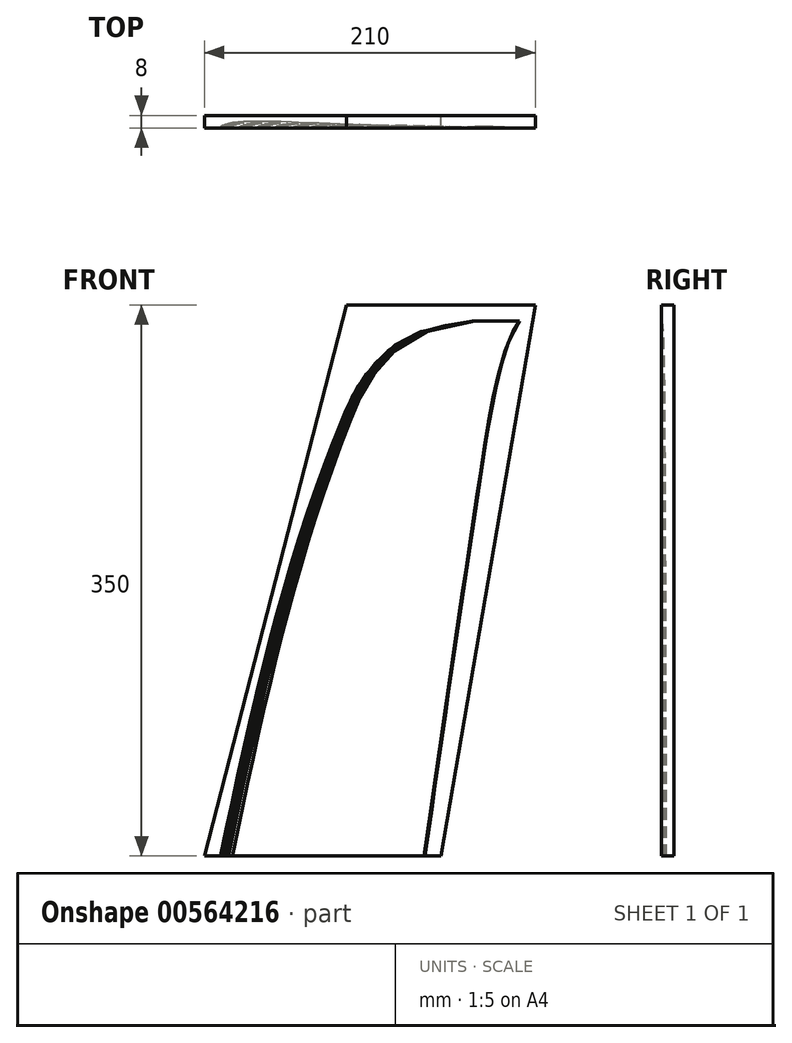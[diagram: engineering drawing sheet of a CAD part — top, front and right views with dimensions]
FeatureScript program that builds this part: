
annotation { "Feature Type Name" : "Feature", "Feature Type Description" : "" }
export const myFeature = defineFeature(function(context is Context, id is Id, definition is map)
    precondition{}
    {
        {
            var Q0;
            Q0=qCreatedBy(makeId("Top.planeOp"),FACE);
            cPlane(context, id + "F0", {"entities" : qUnion([Q0]), "cplaneType" : CPlaneType.OFFSET, "offset" : 250 * mm, "width" : 150 * mm, "height" : 150 * mm});
        }
        {
            var Q0;
            Q0=qCreatedBy(makeId("Top.planeOp"),FACE);
            cPlane(context, id + "F1", {"entities" : qUnion([Q0]), "cplaneType" : CPlaneType.OFFSET, "offset" : 300 * mm, "width" : 150 * mm, "height" : 150 * mm});
        }
        {
            var Q0;
            Q0=qCreatedBy(makeId("Top.planeOp"),FACE);
            cPlane(context, id + "F2", {"entities" : qUnion([Q0]), "cplaneType" : CPlaneType.OFFSET, "offset" : 320 * mm, "width" : 150 * mm, "height" : 150 * mm});
        }
        {
            var Q0;
            Q0=qCreatedBy(makeId("Top.planeOp"),FACE);
            cPlane(context, id + "F3", {"entities" : qUnion([Q0]), "cplaneType" : CPlaneType.OFFSET, "offset" : 340 * mm, "width" : 150 * mm, "height" : 150 * mm});
        }
        {
            var Q0;
            Q0=qCreatedBy(makeId("Top.planeOp"),FACE);
            var sketch = newSketch(context, id + "F4", { "sketchPlane" : qUnion([Q0])});
            skLineSegment(sketch, "E0", {"start": v(130, 0.16) * mm, "end": v(129.46, 0.15) * mm});
            skLineSegment(sketch, "E1", {"start": v(129.46, 0.15) * mm, "end": v(128.28, 0.22) * mm});
            skLineSegment(sketch, "E2", {"start": v(128.28, 0.22) * mm, "end": v(126.06, 0.3) * mm});
            skLineSegment(sketch, "E3", {"start": v(126.06, 0.3) * mm, "end": v(123.2, 0.44) * mm});
            skLineSegment(sketch, "E4", {"start": v(123.2, 0.44) * mm, "end": v(119.45, 0.6) * mm});
            skLineSegment(sketch, "E5", {"start": v(119.45, 0.6) * mm, "end": v(115.33, 0.75) * mm});
            skLineSegment(sketch, "E6", {"start": v(115.33, 0.75) * mm, "end": v(110.89, 0.96) * mm});
            skLineSegment(sketch, "E7", {"start": v(110.89, 0.96) * mm, "end": v(106, 1.14) * mm});
            skLineSegment(sketch, "E8", {"start": v(106, 1.14) * mm, "end": v(100.37, 1.42) * mm});
            skLineSegment(sketch, "E9", {"start": v(100.37, 1.42) * mm, "end": v(94.84, 1.6) * mm});
            skLineSegment(sketch, "E10", {"start": v(94.84, 1.6) * mm, "end": v(89.05, 1.89) * mm});
            skLineSegment(sketch, "E11", {"start": v(89.05, 1.89) * mm, "end": v(82.47, 2.15) * mm});
            skLineSegment(sketch, "E12", {"start": v(82.47, 2.15) * mm, "end": v(76.13, 2.4) * mm});
            skLineSegment(sketch, "E13", {"start": v(76.13, 2.4) * mm, "end": v(69.53, 2.68) * mm});
            skLineSegment(sketch, "E14", {"start": v(69.53, 2.68) * mm, "end": v(62.6, 3.03) * mm});
            skLineSegment(sketch, "E15", {"start": v(62.6, 3.03) * mm, "end": v(56.55, 3.26) * mm});
            skLineSegment(sketch, "E16", {"start": v(56.55, 3.26) * mm, "end": v(49.78, 3.57) * mm});
            skLineSegment(sketch, "E17", {"start": v(49.78, 3.57) * mm, "end": v(45.16, 3.74) * mm});
            skLineSegment(sketch, "E18", {"start": v(45.16, 3.74) * mm, "end": v(38.39, 3.98) * mm});
            skLineSegment(sketch, "E19", {"start": v(38.39, 3.98) * mm, "end": v(33.66, 4.1) * mm});
            skLineSegment(sketch, "E20", {"start": v(33.66, 4.1) * mm, "end": v(28.01, 4.2) * mm});
            skLineSegment(sketch, "E21", {"start": v(28.01, 4.2) * mm, "end": v(23.16, 4.22) * mm});
            skLineSegment(sketch, "E22", {"start": v(23.16, 4.22) * mm, "end": v(18.3, 4.15) * mm});
            skLineSegment(sketch, "E23", {"start": v(18.3, 4.15) * mm, "end": v(14.57, 4) * mm});
            skLineSegment(sketch, "E24", {"start": v(14.57, 4) * mm, "end": v(11.21, 3.75) * mm});
            skLineSegment(sketch, "E25", {"start": v(11.21, 3.75) * mm, "end": v(7.63, 3.34) * mm});
            skLineSegment(sketch, "E26", {"start": v(7.63, 3.34) * mm, "end": v(5.05, 2.89) * mm});
            skLineSegment(sketch, "E27", {"start": v(5.05, 2.89) * mm, "end": v(2.92, 2.28) * mm});
            skLineSegment(sketch, "E28", {"start": v(2.92, 2.28) * mm, "end": v(1.32, 1.56) * mm});
            skLineSegment(sketch, "E29", {"start": v(1.32, 1.56) * mm, "end": v(0.49, 0.98) * mm});
            skLineSegment(sketch, "E30", {"start": v(0.49, 0.98) * mm, "end": v(0.08, 0.4) * mm});
            skLineSegment(sketch, "E31", {"start": v(0.08, 0.4) * mm, "end": v(0, 0) * mm});
            skLineSegment(sketch, "E32", {"start": v(0, 0) * mm, "end": v(0.03, -0.22) * mm});
            skLineSegment(sketch, "E33", {"start": v(0.03, -0.22) * mm, "end": v(0.08, -0.45) * mm});
            skLineSegment(sketch, "E34", {"start": v(0.08, -0.45) * mm, "end": v(0.22, -0.67) * mm});
            skLineSegment(sketch, "E35", {"start": v(0.22, -0.67) * mm, "end": v(1, -1.38) * mm});
            skLineSegment(sketch, "E36", {"start": v(1, -1.38) * mm, "end": v(2.07, -1.93) * mm});
            skLineSegment(sketch, "E37", {"start": v(2.07, -1.93) * mm, "end": v(3.73, -2.53) * mm});
            skLineSegment(sketch, "E38", {"start": v(3.73, -2.53) * mm, "end": v(6.34, -3.13) * mm});
            skLineSegment(sketch, "E39", {"start": v(6.34, -3.13) * mm, "end": v(9.36, -3.57) * mm});
            skLineSegment(sketch, "E40", {"start": v(9.36, -3.57) * mm, "end": v(13.18, -3.91) * mm});
            skLineSegment(sketch, "E41", {"start": v(13.18, -3.91) * mm, "end": v(17.57, -4.14) * mm});
            skLineSegment(sketch, "E42", {"start": v(17.57, -4.14) * mm, "end": v(22.67, -4.2) * mm});
            skLineSegment(sketch, "E43", {"start": v(22.67, -4.2) * mm, "end": v(28.18, -4.22) * mm});
            skLineSegment(sketch, "E44", {"start": v(28.18, -4.22) * mm, "end": v(34.02, -4.06) * mm});
            skLineSegment(sketch, "E45", {"start": v(34.02, -4.06) * mm, "end": v(40.18, -3.88) * mm});
            skLineSegment(sketch, "E46", {"start": v(40.18, -3.88) * mm, "end": v(46.73, -3.67) * mm});
            skLineSegment(sketch, "E47", {"start": v(46.73, -3.67) * mm, "end": v(53.52, -3.4) * mm});
            skLineSegment(sketch, "E48", {"start": v(53.52, -3.4) * mm, "end": v(61.2, -3.04) * mm});
            skLineSegment(sketch, "E49", {"start": v(61.2, -3.04) * mm, "end": v(67.7, -2.76) * mm});
            skLineSegment(sketch, "E50", {"start": v(67.7, -2.76) * mm, "end": v(74.25, -2.49) * mm});
            skLineSegment(sketch, "E51", {"start": v(74.25, -2.49) * mm, "end": v(81.45, -2.17) * mm});
            skLineSegment(sketch, "E52", {"start": v(81.45, -2.17) * mm, "end": v(88.16, -1.9) * mm});
            skLineSegment(sketch, "E53", {"start": v(88.16, -1.9) * mm, "end": v(94.61, -1.62) * mm});
            skLineSegment(sketch, "E54", {"start": v(94.61, -1.62) * mm, "end": v(100.76, -1.37) * mm});
            skLineSegment(sketch, "E55", {"start": v(100.76, -1.37) * mm, "end": v(106.42, -1.13) * mm});
            skLineSegment(sketch, "E56", {"start": v(106.42, -1.13) * mm, "end": v(111.7, -0.9) * mm});
            skLineSegment(sketch, "E57", {"start": v(111.7, -0.9) * mm, "end": v(116.1, -0.72) * mm});
            skLineSegment(sketch, "E58", {"start": v(116.1, -0.72) * mm, "end": v(120.1, -0.54) * mm});
            skLineSegment(sketch, "E59", {"start": v(120.1, -0.54) * mm, "end": v(123.41, -0.43) * mm});
            skLineSegment(sketch, "E60", {"start": v(123.41, -0.43) * mm, "end": v(126.23, -0.29) * mm});
            skLineSegment(sketch, "E61", {"start": v(126.23, -0.29) * mm, "end": v(128.2, -0.2) * mm});
            skLineSegment(sketch, "E62", {"start": v(128.2, -0.2) * mm, "end": v(130, -0.13) * mm});
            skLineSegment(sketch, "E63", {"start": v(130, -0.13) * mm, "end": v(130, 0.16) * mm});
            skSolve(sketch);
        }
        {
            var Q0;
            Q0=qCreatedBy(id+"F0.planeOp",FACE);
            var sketch = newSketch(context, id + "F5", { "sketchPlane" : qUnion([Q0])});
            skLineSegment(sketch, "E64", {"start": v(166.6, 0.13) * mm, "end": v(166.18, 0.12) * mm});
            skLineSegment(sketch, "E65", {"start": v(166.18, 0.12) * mm, "end": v(165.27, 0.17) * mm});
            skLineSegment(sketch, "E66", {"start": v(165.27, 0.17) * mm, "end": v(163.56, 0.23) * mm});
            skLineSegment(sketch, "E67", {"start": v(163.56, 0.23) * mm, "end": v(161.37, 0.33) * mm});
            skLineSegment(sketch, "E68", {"start": v(161.37, 0.33) * mm, "end": v(158.49, 0.46) * mm});
            skLineSegment(sketch, "E69", {"start": v(158.49, 0.46) * mm, "end": v(155.31, 0.58) * mm});
            skLineSegment(sketch, "E70", {"start": v(155.31, 0.58) * mm, "end": v(151.9, 0.74) * mm});
            skLineSegment(sketch, "E71", {"start": v(151.9, 0.74) * mm, "end": v(148.14, 0.88) * mm});
            skLineSegment(sketch, "E72", {"start": v(148.14, 0.88) * mm, "end": v(143.8, 1.1) * mm});
            skLineSegment(sketch, "E73", {"start": v(143.8, 1.1) * mm, "end": v(139.55, 1.24) * mm});
            skLineSegment(sketch, "E74", {"start": v(139.55, 1.24) * mm, "end": v(135.1, 1.45) * mm});
            skLineSegment(sketch, "E75", {"start": v(135.1, 1.45) * mm, "end": v(130.04, 1.65) * mm});
            skLineSegment(sketch, "E76", {"start": v(130.04, 1.65) * mm, "end": v(125.16, 1.85) * mm});
            skLineSegment(sketch, "E77", {"start": v(125.16, 1.85) * mm, "end": v(120.08, 2.06) * mm});
            skLineSegment(sketch, "E78", {"start": v(120.08, 2.06) * mm, "end": v(114.76, 2.33) * mm});
            skLineSegment(sketch, "E79", {"start": v(114.76, 2.33) * mm, "end": v(110.1, 2.5) * mm});
            skLineSegment(sketch, "E80", {"start": v(110.1, 2.5) * mm, "end": v(104.9, 2.75) * mm});
            skLineSegment(sketch, "E81", {"start": v(104.9, 2.75) * mm, "end": v(101.34, 2.88) * mm});
            skLineSegment(sketch, "E82", {"start": v(101.34, 2.88) * mm, "end": v(96.13, 3.06) * mm});
            skLineSegment(sketch, "E83", {"start": v(96.13, 3.06) * mm, "end": v(92.5, 3.16) * mm});
            skLineSegment(sketch, "E84", {"start": v(92.5, 3.16) * mm, "end": v(88.15, 3.23) * mm});
            skLineSegment(sketch, "E85", {"start": v(88.15, 3.23) * mm, "end": v(84.42, 3.24) * mm});
            skLineSegment(sketch, "E86", {"start": v(84.42, 3.24) * mm, "end": v(80.69, 3.19) * mm});
            skLineSegment(sketch, "E87", {"start": v(80.69, 3.19) * mm, "end": v(77.81, 3.08) * mm});
            skLineSegment(sketch, "E88", {"start": v(77.81, 3.08) * mm, "end": v(75.23, 2.89) * mm});
            skLineSegment(sketch, "E89", {"start": v(75.23, 2.89) * mm, "end": v(72.47, 2.57) * mm});
            skLineSegment(sketch, "E90", {"start": v(72.47, 2.57) * mm, "end": v(70.5, 2.22) * mm});
            skLineSegment(sketch, "E91", {"start": v(70.5, 2.22) * mm, "end": v(68.85, 1.76) * mm});
            skLineSegment(sketch, "E92", {"start": v(68.85, 1.76) * mm, "end": v(67.62, 1.2) * mm});
            skLineSegment(sketch, "E93", {"start": v(67.62, 1.2) * mm, "end": v(66.98, 0.75) * mm});
            skLineSegment(sketch, "E94", {"start": v(66.98, 0.75) * mm, "end": v(66.66, 0.3) * mm});
            skLineSegment(sketch, "E95", {"start": v(66.66, 0.3) * mm, "end": v(66.6, 0) * mm});
            skLineSegment(sketch, "E96", {"start": v(66.6, 0) * mm, "end": v(66.62, -0.17) * mm});
            skLineSegment(sketch, "E97", {"start": v(66.62, -0.17) * mm, "end": v(66.66, -0.35) * mm});
            skLineSegment(sketch, "E98", {"start": v(66.66, -0.35) * mm, "end": v(66.78, -0.52) * mm});
            skLineSegment(sketch, "E99", {"start": v(66.78, -0.52) * mm, "end": v(67.37, -1.06) * mm});
            skLineSegment(sketch, "E100", {"start": v(67.37, -1.06) * mm, "end": v(68.2, -1.48) * mm});
            skLineSegment(sketch, "E101", {"start": v(68.2, -1.48) * mm, "end": v(69.47, -1.95) * mm});
            skLineSegment(sketch, "E102", {"start": v(69.47, -1.95) * mm, "end": v(71.48, -2.4) * mm});
            skLineSegment(sketch, "E103", {"start": v(71.48, -2.4) * mm, "end": v(73.8, -2.74) * mm});
            skLineSegment(sketch, "E104", {"start": v(73.8, -2.74) * mm, "end": v(76.75, -3) * mm});
            skLineSegment(sketch, "E105", {"start": v(76.75, -3) * mm, "end": v(80.12, -3.18) * mm});
            skLineSegment(sketch, "E106", {"start": v(80.12, -3.18) * mm, "end": v(84.04, -3.23) * mm});
            skLineSegment(sketch, "E107", {"start": v(84.04, -3.23) * mm, "end": v(88.28, -3.24) * mm});
            skLineSegment(sketch, "E108", {"start": v(88.28, -3.24) * mm, "end": v(92.77, -3.12) * mm});
            skLineSegment(sketch, "E109", {"start": v(92.77, -3.12) * mm, "end": v(97.5, -2.99) * mm});
            skLineSegment(sketch, "E110", {"start": v(97.5, -2.99) * mm, "end": v(102.55, -2.82) * mm});
            skLineSegment(sketch, "E111", {"start": v(102.55, -2.82) * mm, "end": v(107.77, -2.62) * mm});
            skLineSegment(sketch, "E112", {"start": v(107.77, -2.62) * mm, "end": v(113.67, -2.34) * mm});
            skLineSegment(sketch, "E113", {"start": v(113.67, -2.34) * mm, "end": v(118.68, -2.12) * mm});
            skLineSegment(sketch, "E114", {"start": v(118.68, -2.12) * mm, "end": v(123.72, -1.91) * mm});
            skLineSegment(sketch, "E115", {"start": v(123.72, -1.91) * mm, "end": v(129.25, -1.67) * mm});
            skLineSegment(sketch, "E116", {"start": v(129.25, -1.67) * mm, "end": v(134.41, -1.46) * mm});
            skLineSegment(sketch, "E117", {"start": v(134.41, -1.46) * mm, "end": v(139.38, -1.24) * mm});
            skLineSegment(sketch, "E118", {"start": v(139.38, -1.24) * mm, "end": v(144.1, -1.06) * mm});
            skLineSegment(sketch, "E119", {"start": v(144.1, -1.06) * mm, "end": v(148.46, -0.87) * mm});
            skLineSegment(sketch, "E120", {"start": v(148.46, -0.87) * mm, "end": v(152.52, -0.7) * mm});
            skLineSegment(sketch, "E121", {"start": v(152.52, -0.7) * mm, "end": v(155.91, -0.56) * mm});
            skLineSegment(sketch, "E122", {"start": v(155.91, -0.56) * mm, "end": v(158.99, -0.42) * mm});
            skLineSegment(sketch, "E123", {"start": v(158.99, -0.42) * mm, "end": v(161.53, -0.33) * mm});
            skLineSegment(sketch, "E124", {"start": v(161.53, -0.33) * mm, "end": v(163.7, -0.22) * mm});
            skLineSegment(sketch, "E125", {"start": v(163.7, -0.22) * mm, "end": v(165.2, -0.15) * mm});
            skLineSegment(sketch, "E126", {"start": v(165.2, -0.15) * mm, "end": v(166.6, -0.1) * mm});
            skLineSegment(sketch, "E127", {"start": v(166.6, -0.1) * mm, "end": v(166.6, 0.13) * mm});
            skSolve(sketch);
        }
        {
            var Q0;
            Q0=qCreatedBy(id+"F1.planeOp",FACE);
            var sketch = newSketch(context, id + "F6", { "sketchPlane" : qUnion([Q0])});
            skLineSegment(sketch, "E128", {"start": v(175.53, 0.1) * mm, "end": v(175.16, 0.1) * mm});
            skLineSegment(sketch, "E129", {"start": v(175.16, 0.1) * mm, "end": v(174.37, 0.15) * mm});
            skLineSegment(sketch, "E130", {"start": v(174.37, 0.15) * mm, "end": v(172.88, 0.2) * mm});
            skLineSegment(sketch, "E131", {"start": v(172.88, 0.2) * mm, "end": v(170.98, 0.3) * mm});
            skLineSegment(sketch, "E132", {"start": v(170.98, 0.3) * mm, "end": v(168.46, 0.4) * mm});
            skLineSegment(sketch, "E133", {"start": v(168.46, 0.4) * mm, "end": v(165.7, 0.5) * mm});
            skLineSegment(sketch, "E134", {"start": v(165.7, 0.5) * mm, "end": v(162.73, 0.64) * mm});
            skLineSegment(sketch, "E135", {"start": v(162.73, 0.64) * mm, "end": v(159.46, 0.76) * mm});
            skLineSegment(sketch, "E136", {"start": v(159.46, 0.76) * mm, "end": v(155.68, 0.95) * mm});
            skLineSegment(sketch, "E137", {"start": v(155.68, 0.95) * mm, "end": v(151.98, 1.08) * mm});
            skLineSegment(sketch, "E138", {"start": v(151.98, 1.08) * mm, "end": v(148.1, 1.26) * mm});
            skLineSegment(sketch, "E139", {"start": v(148.1, 1.26) * mm, "end": v(143.7, 1.44) * mm});
            skLineSegment(sketch, "E140", {"start": v(143.7, 1.44) * mm, "end": v(139.45, 1.61) * mm});
            skLineSegment(sketch, "E141", {"start": v(139.45, 1.61) * mm, "end": v(135.03, 1.8) * mm});
            skLineSegment(sketch, "E142", {"start": v(135.03, 1.8) * mm, "end": v(130.4, 2.03) * mm});
            skLineSegment(sketch, "E143", {"start": v(130.4, 2.03) * mm, "end": v(126.34, 2.18) * mm});
            skLineSegment(sketch, "E144", {"start": v(126.34, 2.18) * mm, "end": v(121.81, 2.4) * mm});
            skLineSegment(sketch, "E145", {"start": v(121.81, 2.4) * mm, "end": v(118.72, 2.5) * mm});
            skLineSegment(sketch, "E146", {"start": v(118.72, 2.5) * mm, "end": v(114.18, 2.66) * mm});
            skLineSegment(sketch, "E147", {"start": v(114.18, 2.66) * mm, "end": v(111.02, 2.75) * mm});
            skLineSegment(sketch, "E148", {"start": v(111.02, 2.75) * mm, "end": v(107.23, 2.81) * mm});
            skLineSegment(sketch, "E149", {"start": v(107.23, 2.81) * mm, "end": v(103.99, 2.82) * mm});
            skLineSegment(sketch, "E150", {"start": v(103.99, 2.82) * mm, "end": v(100.74, 2.78) * mm});
            skLineSegment(sketch, "E151", {"start": v(100.74, 2.78) * mm, "end": v(98.23, 2.68) * mm});
            skLineSegment(sketch, "E152", {"start": v(98.23, 2.68) * mm, "end": v(95.99, 2.51) * mm});
            skLineSegment(sketch, "E153", {"start": v(95.99, 2.51) * mm, "end": v(93.58, 2.24) * mm});
            skLineSegment(sketch, "E154", {"start": v(93.58, 2.24) * mm, "end": v(91.86, 1.93) * mm});
            skLineSegment(sketch, "E155", {"start": v(91.86, 1.93) * mm, "end": v(90.43, 1.53) * mm});
            skLineSegment(sketch, "E156", {"start": v(90.43, 1.53) * mm, "end": v(89.36, 1.04) * mm});
            skLineSegment(sketch, "E157", {"start": v(89.36, 1.04) * mm, "end": v(88.8, 0.65) * mm});
            skLineSegment(sketch, "E158", {"start": v(88.8, 0.65) * mm, "end": v(88.53, 0.27) * mm});
            skLineSegment(sketch, "E159", {"start": v(88.53, 0.27) * mm, "end": v(88.47, 0) * mm});
            skLineSegment(sketch, "E160", {"start": v(88.47, 0) * mm, "end": v(88.5, -0.15) * mm});
            skLineSegment(sketch, "E161", {"start": v(88.5, -0.15) * mm, "end": v(88.53, -0.3) * mm});
            skLineSegment(sketch, "E162", {"start": v(88.53, -0.3) * mm, "end": v(88.63, -0.45) * mm});
            skLineSegment(sketch, "E163", {"start": v(88.63, -0.45) * mm, "end": v(89.14, -0.93) * mm});
            skLineSegment(sketch, "E164", {"start": v(89.14, -0.93) * mm, "end": v(89.86, -1.3) * mm});
            skLineSegment(sketch, "E165", {"start": v(89.86, -1.3) * mm, "end": v(90.98, -1.7) * mm});
            skLineSegment(sketch, "E166", {"start": v(90.98, -1.7) * mm, "end": v(92.72, -2.1) * mm});
            skLineSegment(sketch, "E167", {"start": v(92.72, -2.1) * mm, "end": v(94.75, -2.39) * mm});
            skLineSegment(sketch, "E168", {"start": v(94.75, -2.39) * mm, "end": v(97.3, -2.62) * mm});
            skLineSegment(sketch, "E169", {"start": v(97.3, -2.62) * mm, "end": v(100.24, -2.77) * mm});
            skLineSegment(sketch, "E170", {"start": v(100.24, -2.77) * mm, "end": v(103.66, -2.8) * mm});
            skLineSegment(sketch, "E171", {"start": v(103.66, -2.8) * mm, "end": v(107.34, -2.82) * mm});
            skLineSegment(sketch, "E172", {"start": v(107.34, -2.82) * mm, "end": v(111.26, -2.72) * mm});
            skLineSegment(sketch, "E173", {"start": v(111.26, -2.72) * mm, "end": v(115.38, -2.6) * mm});
            skLineSegment(sketch, "E174", {"start": v(115.38, -2.6) * mm, "end": v(119.77, -2.46) * mm});
            skLineSegment(sketch, "E175", {"start": v(119.77, -2.46) * mm, "end": v(124.31, -2.28) * mm});
            skLineSegment(sketch, "E176", {"start": v(124.31, -2.28) * mm, "end": v(129.45, -2.03) * mm});
            skLineSegment(sketch, "E177", {"start": v(129.45, -2.03) * mm, "end": v(133.81, -1.85) * mm});
            skLineSegment(sketch, "E178", {"start": v(133.81, -1.85) * mm, "end": v(138.2, -1.66) * mm});
            skLineSegment(sketch, "E179", {"start": v(138.2, -1.66) * mm, "end": v(143.02, -1.45) * mm});
            skLineSegment(sketch, "E180", {"start": v(143.02, -1.45) * mm, "end": v(147.5, -1.28) * mm});
            skLineSegment(sketch, "E181", {"start": v(147.5, -1.28) * mm, "end": v(151.83, -1.08) * mm});
            skLineSegment(sketch, "E182", {"start": v(151.83, -1.08) * mm, "end": v(155.95, -0.92) * mm});
            skLineSegment(sketch, "E183", {"start": v(155.95, -0.92) * mm, "end": v(159.74, -0.76) * mm});
            skLineSegment(sketch, "E184", {"start": v(159.74, -0.76) * mm, "end": v(163.27, -0.6) * mm});
            skLineSegment(sketch, "E185", {"start": v(163.27, -0.6) * mm, "end": v(166.22, -0.48) * mm});
            skLineSegment(sketch, "E186", {"start": v(166.22, -0.48) * mm, "end": v(168.9, -0.36) * mm});
            skLineSegment(sketch, "E187", {"start": v(168.9, -0.36) * mm, "end": v(171.11, -0.29) * mm});
            skLineSegment(sketch, "E188", {"start": v(171.11, -0.29) * mm, "end": v(173, -0.2) * mm});
            skLineSegment(sketch, "E189", {"start": v(173, -0.2) * mm, "end": v(174.32, -0.13) * mm});
            skLineSegment(sketch, "E190", {"start": v(174.32, -0.13) * mm, "end": v(175.53, -0.09) * mm});
            skLineSegment(sketch, "E191", {"start": v(175.53, -0.09) * mm, "end": v(175.53, 0.1) * mm});
            skSolve(sketch);
        }
        {
            var Q0;
            Q0=qCreatedBy(id+"F2.planeOp",FACE);
            var sketch = newSketch(context, id + "F7", { "sketchPlane" : qUnion([Q0])});
            skLineSegment(sketch, "E192", {"start": v(180.66, 0.1) * mm, "end": v(180.34, 0.09) * mm});
            skLineSegment(sketch, "E193", {"start": v(180.34, 0.09) * mm, "end": v(179.66, 0.13) * mm});
            skLineSegment(sketch, "E194", {"start": v(179.66, 0.13) * mm, "end": v(178.37, 0.17) * mm});
            skLineSegment(sketch, "E195", {"start": v(178.37, 0.17) * mm, "end": v(176.72, 0.25) * mm});
            skLineSegment(sketch, "E196", {"start": v(176.72, 0.25) * mm, "end": v(174.55, 0.34) * mm});
            skLineSegment(sketch, "E197", {"start": v(174.55, 0.34) * mm, "end": v(172.16, 0.44) * mm});
            skLineSegment(sketch, "E198", {"start": v(172.16, 0.44) * mm, "end": v(169.58, 0.55) * mm});
            skLineSegment(sketch, "E199", {"start": v(169.58, 0.55) * mm, "end": v(166.75, 0.66) * mm});
            skLineSegment(sketch, "E200", {"start": v(166.75, 0.66) * mm, "end": v(163.49, 0.82) * mm});
            skLineSegment(sketch, "E201", {"start": v(163.49, 0.82) * mm, "end": v(160.28, 0.93) * mm});
            skLineSegment(sketch, "E202", {"start": v(160.28, 0.93) * mm, "end": v(156.93, 1.1) * mm});
            skLineSegment(sketch, "E203", {"start": v(156.93, 1.1) * mm, "end": v(153.12, 1.25) * mm});
            skLineSegment(sketch, "E204", {"start": v(153.12, 1.25) * mm, "end": v(149.45, 1.4) * mm});
            skLineSegment(sketch, "E205", {"start": v(149.45, 1.4) * mm, "end": v(145.62, 1.55) * mm});
            skLineSegment(sketch, "E206", {"start": v(145.62, 1.55) * mm, "end": v(141.61, 1.76) * mm});
            skLineSegment(sketch, "E207", {"start": v(141.61, 1.76) * mm, "end": v(138.1, 1.89) * mm});
            skLineSegment(sketch, "E208", {"start": v(138.1, 1.89) * mm, "end": v(134.19, 2.07) * mm});
            skLineSegment(sketch, "E209", {"start": v(134.19, 2.07) * mm, "end": v(131.5, 2.17) * mm});
            skLineSegment(sketch, "E210", {"start": v(131.5, 2.17) * mm, "end": v(127.58, 2.3) * mm});
            skLineSegment(sketch, "E211", {"start": v(127.58, 2.3) * mm, "end": v(124.85, 2.38) * mm});
            skLineSegment(sketch, "E212", {"start": v(124.85, 2.38) * mm, "end": v(121.57, 2.43) * mm});
            skLineSegment(sketch, "E213", {"start": v(121.57, 2.43) * mm, "end": v(118.76, 2.44) * mm});
            skLineSegment(sketch, "E214", {"start": v(118.76, 2.44) * mm, "end": v(115.95, 2.4) * mm});
            skLineSegment(sketch, "E215", {"start": v(115.95, 2.4) * mm, "end": v(113.79, 2.32) * mm});
            skLineSegment(sketch, "E216", {"start": v(113.79, 2.32) * mm, "end": v(111.84, 2.17) * mm});
            skLineSegment(sketch, "E217", {"start": v(111.84, 2.17) * mm, "end": v(109.76, 1.93) * mm});
            skLineSegment(sketch, "E218", {"start": v(109.76, 1.93) * mm, "end": v(108.27, 1.67) * mm});
            skLineSegment(sketch, "E219", {"start": v(108.27, 1.67) * mm, "end": v(107.04, 1.32) * mm});
            skLineSegment(sketch, "E220", {"start": v(107.04, 1.32) * mm, "end": v(106.1, 0.9) * mm});
            skLineSegment(sketch, "E221", {"start": v(106.1, 0.9) * mm, "end": v(105.63, 0.57) * mm});
            skLineSegment(sketch, "E222", {"start": v(105.63, 0.57) * mm, "end": v(105.39, 0.23) * mm});
            skLineSegment(sketch, "E223", {"start": v(105.39, 0.23) * mm, "end": v(105.34, 0) * mm});
            skLineSegment(sketch, "E224", {"start": v(105.34, 0) * mm, "end": v(105.36, -0.13) * mm});
            skLineSegment(sketch, "E225", {"start": v(105.36, -0.13) * mm, "end": v(105.39, -0.26) * mm});
            skLineSegment(sketch, "E226", {"start": v(105.39, -0.26) * mm, "end": v(105.47, -0.39) * mm});
            skLineSegment(sketch, "E227", {"start": v(105.47, -0.39) * mm, "end": v(105.92, -0.8) * mm});
            skLineSegment(sketch, "E228", {"start": v(105.92, -0.8) * mm, "end": v(106.54, -1.12) * mm});
            skLineSegment(sketch, "E229", {"start": v(106.54, -1.12) * mm, "end": v(107.5, -1.47) * mm});
            skLineSegment(sketch, "E230", {"start": v(107.5, -1.47) * mm, "end": v(109.02, -1.81) * mm});
            skLineSegment(sketch, "E231", {"start": v(109.02, -1.81) * mm, "end": v(110.77, -2.07) * mm});
            skLineSegment(sketch, "E232", {"start": v(110.77, -2.07) * mm, "end": v(112.98, -2.27) * mm});
            skLineSegment(sketch, "E233", {"start": v(112.98, -2.27) * mm, "end": v(115.52, -2.4) * mm});
            skLineSegment(sketch, "E234", {"start": v(115.52, -2.4) * mm, "end": v(118.48, -2.43) * mm});
            skLineSegment(sketch, "E235", {"start": v(118.48, -2.43) * mm, "end": v(121.67, -2.44) * mm});
            skLineSegment(sketch, "E236", {"start": v(121.67, -2.44) * mm, "end": v(125.06, -2.35) * mm});
            skLineSegment(sketch, "E237", {"start": v(125.06, -2.35) * mm, "end": v(128.62, -2.25) * mm});
            skLineSegment(sketch, "E238", {"start": v(128.62, -2.25) * mm, "end": v(132.42, -2.13) * mm});
            skLineSegment(sketch, "E239", {"start": v(132.42, -2.13) * mm, "end": v(136.35, -1.97) * mm});
            skLineSegment(sketch, "E240", {"start": v(136.35, -1.97) * mm, "end": v(140.8, -1.76) * mm});
            skLineSegment(sketch, "E241", {"start": v(140.8, -1.76) * mm, "end": v(144.57, -1.6) * mm});
            skLineSegment(sketch, "E242", {"start": v(144.57, -1.6) * mm, "end": v(148.36, -1.44) * mm});
            skLineSegment(sketch, "E243", {"start": v(148.36, -1.44) * mm, "end": v(152.53, -1.26) * mm});
            skLineSegment(sketch, "E244", {"start": v(152.53, -1.26) * mm, "end": v(156.41, -1.1) * mm});
            skLineSegment(sketch, "E245", {"start": v(156.41, -1.1) * mm, "end": v(160.16, -0.94) * mm});
            skLineSegment(sketch, "E246", {"start": v(160.16, -0.94) * mm, "end": v(163.72, -0.8) * mm});
            skLineSegment(sketch, "E247", {"start": v(163.72, -0.8) * mm, "end": v(167, -0.65) * mm});
            skLineSegment(sketch, "E248", {"start": v(167, -0.65) * mm, "end": v(170.05, -0.53) * mm});
            skLineSegment(sketch, "E249", {"start": v(170.05, -0.53) * mm, "end": v(172.6, -0.42) * mm});
            skLineSegment(sketch, "E250", {"start": v(172.6, -0.42) * mm, "end": v(174.92, -0.31) * mm});
            skLineSegment(sketch, "E251", {"start": v(174.92, -0.31) * mm, "end": v(176.84, -0.25) * mm});
            skLineSegment(sketch, "E252", {"start": v(176.84, -0.25) * mm, "end": v(178.47, -0.17) * mm});
            skLineSegment(sketch, "E253", {"start": v(178.47, -0.17) * mm, "end": v(179.61, -0.12) * mm});
            skLineSegment(sketch, "E254", {"start": v(179.61, -0.12) * mm, "end": v(180.66, -0.08) * mm});
            skLineSegment(sketch, "E255", {"start": v(180.66, -0.08) * mm, "end": v(180.66, 0.1) * mm});
            skSolve(sketch);
        }
        {
            var Q0;
            Q0=qCreatedBy(id+"F3.planeOp",FACE);
            var sketch = newSketch(context, id + "F8", { "sketchPlane" : qUnion([Q0])});
            skLineSegment(sketch, "E256", {"start": v(190, 0.04) * mm, "end": v(189.88, 0.03) * mm});
            skLineSegment(sketch, "E257", {"start": v(189.88, 0.03) * mm, "end": v(189.6, 0.05) * mm});
            skLineSegment(sketch, "E258", {"start": v(189.6, 0.05) * mm, "end": v(189.1, 0.07) * mm});
            skLineSegment(sketch, "E259", {"start": v(189.1, 0.07) * mm, "end": v(188.44, 0.1) * mm});
            skLineSegment(sketch, "E260", {"start": v(188.44, 0.1) * mm, "end": v(187.57, 0.14) * mm});
            skLineSegment(sketch, "E261", {"start": v(187.57, 0.14) * mm, "end": v(186.62, 0.17) * mm});
            skLineSegment(sketch, "E262", {"start": v(186.62, 0.17) * mm, "end": v(185.6, 0.22) * mm});
            skLineSegment(sketch, "E263", {"start": v(185.6, 0.22) * mm, "end": v(184.46, 0.26) * mm});
            skLineSegment(sketch, "E264", {"start": v(184.46, 0.26) * mm, "end": v(183.16, 0.33) * mm});
            skLineSegment(sketch, "E265", {"start": v(183.16, 0.33) * mm, "end": v(181.89, 0.37) * mm});
            skLineSegment(sketch, "E266", {"start": v(181.89, 0.37) * mm, "end": v(180.55, 0.44) * mm});
            skLineSegment(sketch, "E267", {"start": v(180.55, 0.44) * mm, "end": v(179.03, 0.5) * mm});
            skLineSegment(sketch, "E268", {"start": v(179.03, 0.5) * mm, "end": v(177.57, 0.56) * mm});
            skLineSegment(sketch, "E269", {"start": v(177.57, 0.56) * mm, "end": v(176.05, 0.62) * mm});
            skLineSegment(sketch, "E270", {"start": v(176.05, 0.62) * mm, "end": v(174.45, 0.7) * mm});
            skLineSegment(sketch, "E271", {"start": v(174.45, 0.7) * mm, "end": v(173.05, 0.75) * mm});
            skLineSegment(sketch, "E272", {"start": v(173.05, 0.75) * mm, "end": v(171.49, 0.82) * mm});
            skLineSegment(sketch, "E273", {"start": v(171.49, 0.82) * mm, "end": v(170.42, 0.86) * mm});
            skLineSegment(sketch, "E274", {"start": v(170.42, 0.86) * mm, "end": v(168.86, 0.92) * mm});
            skLineSegment(sketch, "E275", {"start": v(168.86, 0.92) * mm, "end": v(167.77, 0.95) * mm});
            skLineSegment(sketch, "E276", {"start": v(167.77, 0.95) * mm, "end": v(166.46, 0.97) * mm});
            skLineSegment(sketch, "E277", {"start": v(166.46, 0.97) * mm, "end": v(165.34, 0.97) * mm});
            skLineSegment(sketch, "E278", {"start": v(165.34, 0.97) * mm, "end": v(164.22, 0.96) * mm});
            skLineSegment(sketch, "E279", {"start": v(164.22, 0.96) * mm, "end": v(163.36, 0.92) * mm});
            skLineSegment(sketch, "E280", {"start": v(163.36, 0.92) * mm, "end": v(162.59, 0.87) * mm});
            skLineSegment(sketch, "E281", {"start": v(162.59, 0.87) * mm, "end": v(161.76, 0.77) * mm});
            skLineSegment(sketch, "E282", {"start": v(161.76, 0.77) * mm, "end": v(161.16, 0.67) * mm});
            skLineSegment(sketch, "E283", {"start": v(161.16, 0.67) * mm, "end": v(160.67, 0.53) * mm});
            skLineSegment(sketch, "E284", {"start": v(160.67, 0.53) * mm, "end": v(160.3, 0.36) * mm});
            skLineSegment(sketch, "E285", {"start": v(160.3, 0.36) * mm, "end": v(160.11, 0.23) * mm});
            skLineSegment(sketch, "E286", {"start": v(160.11, 0.23) * mm, "end": v(160.02, 0.1) * mm});
            skLineSegment(sketch, "E287", {"start": v(160.02, 0.1) * mm, "end": v(160, 0) * mm});
            skLineSegment(sketch, "E288", {"start": v(160, 0) * mm, "end": v(160, -0.05) * mm});
            skLineSegment(sketch, "E289", {"start": v(160, -0.05) * mm, "end": v(160.02, -0.1) * mm});
            skLineSegment(sketch, "E290", {"start": v(160.02, -0.1) * mm, "end": v(160.05, -0.15) * mm});
            skLineSegment(sketch, "E291", {"start": v(160.05, -0.15) * mm, "end": v(160.23, -0.32) * mm});
            skLineSegment(sketch, "E292", {"start": v(160.23, -0.32) * mm, "end": v(160.48, -0.45) * mm});
            skLineSegment(sketch, "E293", {"start": v(160.48, -0.45) * mm, "end": v(160.86, -0.59) * mm});
            skLineSegment(sketch, "E294", {"start": v(160.86, -0.59) * mm, "end": v(161.46, -0.72) * mm});
            skLineSegment(sketch, "E295", {"start": v(161.46, -0.72) * mm, "end": v(162.16, -0.82) * mm});
            skLineSegment(sketch, "E296", {"start": v(162.16, -0.82) * mm, "end": v(163.04, -0.9) * mm});
            skLineSegment(sketch, "E297", {"start": v(163.04, -0.9) * mm, "end": v(164.05, -0.95) * mm});
            skLineSegment(sketch, "E298", {"start": v(164.05, -0.95) * mm, "end": v(165.23, -0.97) * mm});
            skLineSegment(sketch, "E299", {"start": v(165.23, -0.97) * mm, "end": v(166.5, -0.97) * mm});
            skLineSegment(sketch, "E300", {"start": v(166.5, -0.97) * mm, "end": v(167.85, -0.94) * mm});
            skLineSegment(sketch, "E301", {"start": v(167.85, -0.94) * mm, "end": v(169.27, -0.9) * mm});
            skLineSegment(sketch, "E302", {"start": v(169.27, -0.9) * mm, "end": v(170.78, -0.85) * mm});
            skLineSegment(sketch, "E303", {"start": v(170.78, -0.85) * mm, "end": v(172.35, -0.79) * mm});
            skLineSegment(sketch, "E304", {"start": v(172.35, -0.79) * mm, "end": v(174.12, -0.7) * mm});
            skLineSegment(sketch, "E305", {"start": v(174.12, -0.7) * mm, "end": v(175.62, -0.64) * mm});
            skLineSegment(sketch, "E306", {"start": v(175.62, -0.64) * mm, "end": v(177.14, -0.57) * mm});
            skLineSegment(sketch, "E307", {"start": v(177.14, -0.57) * mm, "end": v(178.8, -0.5) * mm});
            skLineSegment(sketch, "E308", {"start": v(178.8, -0.5) * mm, "end": v(180.34, -0.44) * mm});
            skLineSegment(sketch, "E309", {"start": v(180.34, -0.44) * mm, "end": v(181.84, -0.37) * mm});
            skLineSegment(sketch, "E310", {"start": v(181.84, -0.37) * mm, "end": v(183.25, -0.32) * mm});
            skLineSegment(sketch, "E311", {"start": v(183.25, -0.32) * mm, "end": v(184.56, -0.26) * mm});
            skLineSegment(sketch, "E312", {"start": v(184.56, -0.26) * mm, "end": v(185.78, -0.2) * mm});
            skLineSegment(sketch, "E313", {"start": v(185.78, -0.2) * mm, "end": v(186.8, -0.17) * mm});
            skLineSegment(sketch, "E314", {"start": v(186.8, -0.17) * mm, "end": v(187.72, -0.12) * mm});
            skLineSegment(sketch, "E315", {"start": v(187.72, -0.12) * mm, "end": v(188.48, -0.1) * mm});
            skLineSegment(sketch, "E316", {"start": v(188.48, -0.1) * mm, "end": v(189.13, -0.07) * mm});
            skLineSegment(sketch, "E317", {"start": v(189.13, -0.07) * mm, "end": v(189.59, -0.05) * mm});
            skLineSegment(sketch, "E318", {"start": v(189.59, -0.05) * mm, "end": v(190, -0.03) * mm});
            skLineSegment(sketch, "E319", {"start": v(190, -0.03) * mm, "end": v(190, 0.04) * mm});
            skSolve(sketch);
        }
        {
            var Q0;
            Q0=qCreatedBy(makeId("Top.planeOp"),FACE);
            cPlane(context, id + "F9", {"entities" : qUnion([Q0]), "cplaneType" : CPlaneType.OFFSET, "offset" : 280 * mm, "width" : 150 * mm, "height" : 150 * mm});
        }
        {
            var Q0;
            Q0=qCreatedBy(makeId("Top.planeOp"),FACE);
            cPlane(context, id + "F10", {"entities" : qUnion([Q0]), "cplaneType" : CPlaneType.OFFSET, "offset" : 330 * mm, "width" : 150 * mm, "height" : 150 * mm});
        }
        {
            var Q0;
            Q0=qCreatedBy(id+"F9.planeOp",FACE);
            var sketch = newSketch(context, id + "F11", { "sketchPlane" : qUnion([Q0])});
            skLineSegment(sketch, "E320", {"start": v(171.51, 0.12) * mm, "end": v(171.12, 0.1) * mm});
            skLineSegment(sketch, "E321", {"start": v(171.12, 0.1) * mm, "end": v(170.28, 0.16) * mm});
            skLineSegment(sketch, "E322", {"start": v(170.28, 0.16) * mm, "end": v(168.69, 0.21) * mm});
            skLineSegment(sketch, "E323", {"start": v(168.69, 0.21) * mm, "end": v(166.65, 0.31) * mm});
            skLineSegment(sketch, "E324", {"start": v(166.65, 0.31) * mm, "end": v(163.96, 0.42) * mm});
            skLineSegment(sketch, "E325", {"start": v(163.96, 0.42) * mm, "end": v(161.01, 0.54) * mm});
            skLineSegment(sketch, "E326", {"start": v(161.01, 0.54) * mm, "end": v(157.83, 0.68) * mm});
            skLineSegment(sketch, "E327", {"start": v(157.83, 0.68) * mm, "end": v(154.34, 0.81) * mm});
            skLineSegment(sketch, "E328", {"start": v(154.34, 0.81) * mm, "end": v(150.3, 1.02) * mm});
            skLineSegment(sketch, "E329", {"start": v(150.3, 1.02) * mm, "end": v(146.35, 1.15) * mm});
            skLineSegment(sketch, "E330", {"start": v(146.35, 1.15) * mm, "end": v(142.2, 1.35) * mm});
            skLineSegment(sketch, "E331", {"start": v(142.2, 1.35) * mm, "end": v(137.5, 1.54) * mm});
            skLineSegment(sketch, "E332", {"start": v(137.5, 1.54) * mm, "end": v(132.96, 1.72) * mm});
            skLineSegment(sketch, "E333", {"start": v(132.96, 1.72) * mm, "end": v(128.24, 1.92) * mm});
            skLineSegment(sketch, "E334", {"start": v(128.24, 1.92) * mm, "end": v(123.29, 2.17) * mm});
            skLineSegment(sketch, "E335", {"start": v(123.29, 2.17) * mm, "end": v(118.95, 2.33) * mm});
            skLineSegment(sketch, "E336", {"start": v(118.95, 2.33) * mm, "end": v(114.11, 2.55) * mm});
            skLineSegment(sketch, "E337", {"start": v(114.11, 2.55) * mm, "end": v(110.8, 2.68) * mm});
            skLineSegment(sketch, "E338", {"start": v(110.8, 2.68) * mm, "end": v(105.96, 2.85) * mm});
            skLineSegment(sketch, "E339", {"start": v(105.96, 2.85) * mm, "end": v(102.58, 2.94) * mm});
            skLineSegment(sketch, "E340", {"start": v(102.58, 2.94) * mm, "end": v(98.54, 3) * mm});
            skLineSegment(sketch, "E341", {"start": v(98.54, 3) * mm, "end": v(95.07, 3.02) * mm});
            skLineSegment(sketch, "E342", {"start": v(95.07, 3.02) * mm, "end": v(91.6, 2.97) * mm});
            skLineSegment(sketch, "E343", {"start": v(91.6, 2.97) * mm, "end": v(88.92, 2.86) * mm});
            skLineSegment(sketch, "E344", {"start": v(88.92, 2.86) * mm, "end": v(86.52, 2.68) * mm});
            skLineSegment(sketch, "E345", {"start": v(86.52, 2.68) * mm, "end": v(83.95, 2.39) * mm});
            skLineSegment(sketch, "E346", {"start": v(83.95, 2.39) * mm, "end": v(82.1, 2.06) * mm});
            skLineSegment(sketch, "E347", {"start": v(82.1, 2.06) * mm, "end": v(80.59, 1.63) * mm});
            skLineSegment(sketch, "E348", {"start": v(80.59, 1.63) * mm, "end": v(79.44, 1.12) * mm});
            skLineSegment(sketch, "E349", {"start": v(79.44, 1.12) * mm, "end": v(78.84, 0.7) * mm});
            skLineSegment(sketch, "E350", {"start": v(78.84, 0.7) * mm, "end": v(78.55, 0.29) * mm});
            skLineSegment(sketch, "E351", {"start": v(78.55, 0.29) * mm, "end": v(78.49, 0) * mm});
            skLineSegment(sketch, "E352", {"start": v(78.49, 0) * mm, "end": v(78.51, -0.16) * mm});
            skLineSegment(sketch, "E353", {"start": v(78.51, -0.16) * mm, "end": v(78.55, -0.33) * mm});
            skLineSegment(sketch, "E354", {"start": v(78.55, -0.33) * mm, "end": v(78.65, -0.48) * mm});
            skLineSegment(sketch, "E355", {"start": v(78.65, -0.48) * mm, "end": v(79.2, -0.99) * mm});
            skLineSegment(sketch, "E356", {"start": v(79.2, -0.99) * mm, "end": v(79.97, -1.38) * mm});
            skLineSegment(sketch, "E357", {"start": v(79.97, -1.38) * mm, "end": v(81.16, -1.81) * mm});
            skLineSegment(sketch, "E358", {"start": v(81.16, -1.81) * mm, "end": v(83.03, -2.24) * mm});
            skLineSegment(sketch, "E359", {"start": v(83.03, -2.24) * mm, "end": v(85.2, -2.55) * mm});
            skLineSegment(sketch, "E360", {"start": v(85.2, -2.55) * mm, "end": v(87.93, -2.8) * mm});
            skLineSegment(sketch, "E361", {"start": v(87.93, -2.8) * mm, "end": v(91.07, -2.96) * mm});
            skLineSegment(sketch, "E362", {"start": v(91.07, -2.96) * mm, "end": v(94.72, -3) * mm});
            skLineSegment(sketch, "E363", {"start": v(94.72, -3) * mm, "end": v(98.65, -3.02) * mm});
            skLineSegment(sketch, "E364", {"start": v(98.65, -3.02) * mm, "end": v(102.84, -2.9) * mm});
            skLineSegment(sketch, "E365", {"start": v(102.84, -2.9) * mm, "end": v(107.24, -2.78) * mm});
            skLineSegment(sketch, "E366", {"start": v(107.24, -2.78) * mm, "end": v(111.93, -2.63) * mm});
            skLineSegment(sketch, "E367", {"start": v(111.93, -2.63) * mm, "end": v(116.78, -2.44) * mm});
            skLineSegment(sketch, "E368", {"start": v(116.78, -2.44) * mm, "end": v(122.28, -2.17) * mm});
            skLineSegment(sketch, "E369", {"start": v(122.28, -2.17) * mm, "end": v(126.93, -1.98) * mm});
            skLineSegment(sketch, "E370", {"start": v(126.93, -1.98) * mm, "end": v(131.62, -1.78) * mm});
            skLineSegment(sketch, "E371", {"start": v(131.62, -1.78) * mm, "end": v(136.77, -1.55) * mm});
            skLineSegment(sketch, "E372", {"start": v(136.77, -1.55) * mm, "end": v(141.57, -1.36) * mm});
            skLineSegment(sketch, "E373", {"start": v(141.57, -1.36) * mm, "end": v(146.19, -1.16) * mm});
            skLineSegment(sketch, "E374", {"start": v(146.19, -1.16) * mm, "end": v(150.59, -0.98) * mm});
            skLineSegment(sketch, "E375", {"start": v(150.59, -0.98) * mm, "end": v(154.64, -0.8) * mm});
            skLineSegment(sketch, "E376", {"start": v(154.64, -0.8) * mm, "end": v(158.41, -0.65) * mm});
            skLineSegment(sketch, "E377", {"start": v(158.41, -0.65) * mm, "end": v(161.57, -0.52) * mm});
            skLineSegment(sketch, "E378", {"start": v(161.57, -0.52) * mm, "end": v(164.43, -0.39) * mm});
            skLineSegment(sketch, "E379", {"start": v(164.43, -0.39) * mm, "end": v(166.8, -0.3) * mm});
            skLineSegment(sketch, "E380", {"start": v(166.8, -0.3) * mm, "end": v(168.8, -0.2) * mm});
            skLineSegment(sketch, "E381", {"start": v(168.8, -0.2) * mm, "end": v(170.22, -0.14) * mm});
            skLineSegment(sketch, "E382", {"start": v(170.22, -0.14) * mm, "end": v(171.51, -0.1) * mm});
            skLineSegment(sketch, "E383", {"start": v(171.51, -0.1) * mm, "end": v(171.51, 0.12) * mm});
            skSolve(sketch);
        }
        {
            var Q0;
            Q0=qCreatedBy(id+"F10.planeOp",FACE);
            var sketch = newSketch(context, id + "F12", { "sketchPlane" : qUnion([Q0])});
            skLineSegment(sketch, "E384", {"start": v(184.5, 0.08) * mm, "end": v(184.23, 0.08) * mm});
            skLineSegment(sketch, "E385", {"start": v(184.23, 0.08) * mm, "end": v(183.64, 0.11) * mm});
            skLineSegment(sketch, "E386", {"start": v(183.64, 0.11) * mm, "end": v(182.53, 0.15) * mm});
            skLineSegment(sketch, "E387", {"start": v(182.53, 0.15) * mm, "end": v(181.1, 0.22) * mm});
            skLineSegment(sketch, "E388", {"start": v(181.1, 0.22) * mm, "end": v(179.23, 0.3) * mm});
            skLineSegment(sketch, "E389", {"start": v(179.23, 0.3) * mm, "end": v(177.16, 0.38) * mm});
            skLineSegment(sketch, "E390", {"start": v(177.16, 0.38) * mm, "end": v(174.94, 0.48) * mm});
            skLineSegment(sketch, "E391", {"start": v(174.94, 0.48) * mm, "end": v(172.5, 0.57) * mm});
            skLineSegment(sketch, "E392", {"start": v(172.5, 0.57) * mm, "end": v(169.68, 0.71) * mm});
            skLineSegment(sketch, "E393", {"start": v(169.68, 0.71) * mm, "end": v(166.92, 0.8) * mm});
            skLineSegment(sketch, "E394", {"start": v(166.92, 0.8) * mm, "end": v(164.02, 0.94) * mm});
            skLineSegment(sketch, "E395", {"start": v(164.02, 0.94) * mm, "end": v(160.73, 1.08) * mm});
            skLineSegment(sketch, "E396", {"start": v(160.73, 1.08) * mm, "end": v(157.56, 1.2) * mm});
            skLineSegment(sketch, "E397", {"start": v(157.56, 1.2) * mm, "end": v(154.26, 1.34) * mm});
            skLineSegment(sketch, "E398", {"start": v(154.26, 1.34) * mm, "end": v(150.8, 1.51) * mm});
            skLineSegment(sketch, "E399", {"start": v(150.8, 1.51) * mm, "end": v(147.77, 1.63) * mm});
            skLineSegment(sketch, "E400", {"start": v(147.77, 1.63) * mm, "end": v(144.4, 1.79) * mm});
            skLineSegment(sketch, "E401", {"start": v(144.4, 1.79) * mm, "end": v(142.08, 1.87) * mm});
            skLineSegment(sketch, "E402", {"start": v(142.08, 1.87) * mm, "end": v(138.7, 1.99) * mm});
            skLineSegment(sketch, "E403", {"start": v(138.7, 1.99) * mm, "end": v(136.33, 2.05) * mm});
            skLineSegment(sketch, "E404", {"start": v(136.33, 2.05) * mm, "end": v(133.5, 2.1) * mm});
            skLineSegment(sketch, "E405", {"start": v(133.5, 2.1) * mm, "end": v(131.08, 2.1) * mm});
            skLineSegment(sketch, "E406", {"start": v(131.08, 2.1) * mm, "end": v(128.66, 2.07) * mm});
            skLineSegment(sketch, "E407", {"start": v(128.66, 2.07) * mm, "end": v(126.79, 2) * mm});
            skLineSegment(sketch, "E408", {"start": v(126.79, 2) * mm, "end": v(125.1, 1.88) * mm});
            skLineSegment(sketch, "E409", {"start": v(125.1, 1.88) * mm, "end": v(123.31, 1.67) * mm});
            skLineSegment(sketch, "E410", {"start": v(123.31, 1.67) * mm, "end": v(122.03, 1.44) * mm});
            skLineSegment(sketch, "E411", {"start": v(122.03, 1.44) * mm, "end": v(120.96, 1.14) * mm});
            skLineSegment(sketch, "E412", {"start": v(120.96, 1.14) * mm, "end": v(120.16, 0.78) * mm});
            skLineSegment(sketch, "E413", {"start": v(120.16, 0.78) * mm, "end": v(119.75, 0.49) * mm});
            skLineSegment(sketch, "E414", {"start": v(119.75, 0.49) * mm, "end": v(119.54, 0.2) * mm});
            skLineSegment(sketch, "E415", {"start": v(119.54, 0.2) * mm, "end": v(119.5, 0) * mm});
            skLineSegment(sketch, "E416", {"start": v(119.5, 0) * mm, "end": v(119.51, -0.1) * mm});
            skLineSegment(sketch, "E417", {"start": v(119.51, -0.1) * mm, "end": v(119.54, -0.23) * mm});
            skLineSegment(sketch, "E418", {"start": v(119.54, -0.23) * mm, "end": v(119.61, -0.34) * mm});
            skLineSegment(sketch, "E419", {"start": v(119.61, -0.34) * mm, "end": v(120, -0.7) * mm});
            skLineSegment(sketch, "E420", {"start": v(120, -0.7) * mm, "end": v(120.54, -0.96) * mm});
            skLineSegment(sketch, "E421", {"start": v(120.54, -0.96) * mm, "end": v(121.37, -1.27) * mm});
            skLineSegment(sketch, "E422", {"start": v(121.37, -1.27) * mm, "end": v(122.67, -1.57) * mm});
            skLineSegment(sketch, "E423", {"start": v(122.67, -1.57) * mm, "end": v(124.18, -1.78) * mm});
            skLineSegment(sketch, "E424", {"start": v(124.18, -1.78) * mm, "end": v(126.1, -1.96) * mm});
            skLineSegment(sketch, "E425", {"start": v(126.1, -1.96) * mm, "end": v(128.29, -2.07) * mm});
            skLineSegment(sketch, "E426", {"start": v(128.29, -2.07) * mm, "end": v(130.84, -2.1) * mm});
            skLineSegment(sketch, "E427", {"start": v(130.84, -2.1) * mm, "end": v(133.59, -2.1) * mm});
            skLineSegment(sketch, "E428", {"start": v(133.59, -2.1) * mm, "end": v(136.51, -2.03) * mm});
            skLineSegment(sketch, "E429", {"start": v(136.51, -2.03) * mm, "end": v(139.6, -1.94) * mm});
            skLineSegment(sketch, "E430", {"start": v(139.6, -1.94) * mm, "end": v(142.87, -1.84) * mm});
            skLineSegment(sketch, "E431", {"start": v(142.87, -1.84) * mm, "end": v(146.26, -1.7) * mm});
            skLineSegment(sketch, "E432", {"start": v(146.26, -1.7) * mm, "end": v(150.1, -1.52) * mm});
            skLineSegment(sketch, "E433", {"start": v(150.1, -1.52) * mm, "end": v(153.35, -1.38) * mm});
            skLineSegment(sketch, "E434", {"start": v(153.35, -1.38) * mm, "end": v(156.63, -1.24) * mm});
            skLineSegment(sketch, "E435", {"start": v(156.63, -1.24) * mm, "end": v(160.22, -1.08) * mm});
            skLineSegment(sketch, "E436", {"start": v(160.22, -1.08) * mm, "end": v(163.58, -0.95) * mm});
            skLineSegment(sketch, "E437", {"start": v(163.58, -0.95) * mm, "end": v(166.8, -0.8) * mm});
            skLineSegment(sketch, "E438", {"start": v(166.8, -0.8) * mm, "end": v(169.88, -0.69) * mm});
            skLineSegment(sketch, "E439", {"start": v(169.88, -0.69) * mm, "end": v(172.7, -0.56) * mm});
            skLineSegment(sketch, "E440", {"start": v(172.7, -0.56) * mm, "end": v(175.35, -0.45) * mm});
            skLineSegment(sketch, "E441", {"start": v(175.35, -0.45) * mm, "end": v(177.55, -0.36) * mm});
            skLineSegment(sketch, "E442", {"start": v(177.55, -0.36) * mm, "end": v(179.55, -0.27) * mm});
            skLineSegment(sketch, "E443", {"start": v(179.55, -0.27) * mm, "end": v(181.2, -0.21) * mm});
            skLineSegment(sketch, "E444", {"start": v(181.2, -0.21) * mm, "end": v(182.61, -0.14) * mm});
            skLineSegment(sketch, "E445", {"start": v(182.61, -0.14) * mm, "end": v(183.6, -0.1) * mm});
            skLineSegment(sketch, "E446", {"start": v(183.6, -0.1) * mm, "end": v(184.5, -0.07) * mm});
            skLineSegment(sketch, "E447", {"start": v(184.5, -0.07) * mm, "end": v(184.5, 0.08) * mm});
            skSolve(sketch);
        }
        {
            var Q0;
            Q0=qSketchRegion(id+"F4",true);
            var Q1;
            Q1=qSketchRegion(id+"F5",true);
            var Q2;
            Q2=qSketchRegion(id+"F11",true);
            var Q3;
            Q3=qSketchRegion(id+"F6",true);
            var Q4;
            Q4=qSketchRegion(id+"F7",true);
            var Q5;
            Q5=qSketchRegion(id+"F12",true);
            var Q6;
            Q6=qSketchRegion(id+"F8",true);
            loft(context, id + "F13", {"sheetProfilesArray" : [{ "sheetProfileEntities" : qUnion([Q0]) }, { "sheetProfileEntities" : qUnion([Q1]) }, { "sheetProfileEntities" : qUnion([Q2]) }, { "sheetProfileEntities" : qUnion([Q3]) }, { "sheetProfileEntities" : qUnion([Q4]) }, { "sheetProfileEntities" : qUnion([Q5]) }, { "sheetProfileEntities" : qUnion([Q6]) }]});
        }
        {
            var Q0;
            Q0=qCreatedBy(makeId("Top.planeOp"),FACE);
            var sketch = newSketch(context, id + "F14", { "sketchPlane" : qUnion([Q0])});
            skLineSegment(sketch, "E448.bottom", {"start": v(-10, 0) * mm, "end": v(140, 0) * mm});
            skLineSegment(sketch, "E448.top", {"start": v(-10, 8) * mm, "end": v(140, 8) * mm});
            skLineSegment(sketch, "E448.left", {"start": v(-10, 0) * mm, "end": v(-10, 8) * mm});
            skLineSegment(sketch, "E448.right", {"start": v(140, 0) * mm, "end": v(140, 8) * mm});
            skSolve(sketch);
        }
        {
            var Q0;
            Q0=qCreatedBy(makeId("Top.planeOp"),FACE);
            cPlane(context, id + "F15", {"entities" : qUnion([Q0]), "cplaneType" : CPlaneType.OFFSET, "offset" : 350 * mm, "width" : 150 * mm, "height" : 150 * mm});
        }
        {
            var Q0;
            Q0=qCreatedBy(id+"F15.planeOp",FACE);
            var sketch = newSketch(context, id + "F16", { "sketchPlane" : qUnion([Q0])});
            skLineSegment(sketch, "E449.bottom", {"start": v(80, 0) * mm, "end": v(200, 0) * mm});
            skLineSegment(sketch, "E449.top", {"start": v(80, 8) * mm, "end": v(200, 8) * mm});
            skLineSegment(sketch, "E449.left", {"start": v(80, 0) * mm, "end": v(80, 8) * mm});
            skLineSegment(sketch, "E449.right", {"start": v(200, 0) * mm, "end": v(200, 8) * mm});
            skSolve(sketch);
        }
        {
            var Q1;
            Q1 = qSketchRegion(id + "F14", true);
            var Q2;
            Q2 = qSketchRegion(id + "F16", true);
            loft(context, id + "F17", {"sheetProfilesArray" : [{ "sheetProfileEntities" : qUnion([Q1]) }, { "sheetProfileEntities" : qUnion([Q2]) }]});
        }
        {
            var Q0;
            Q0=makeQuery(id+"F13.opLoft","SWEPT_BODY",BODY,{"disambiguationData":[OSD([makeQuery(id+"F4.imprint","IMPRINT",FACE,{"disambiguationData":[TD([[makeQuery(id+"F4.imprint","IMPRINT",EDGE,{"derivedFrom":sQuery(id+"F4.wireOp",EDGE,"E0")}),1.0]])]}),sQuery(id+"F5.wireOp",EDGE,"E76"),sQuery(id+"F6.wireOp",EDGE,"E140"),sQuery(id+"F7.wireOp",EDGE,"E204"),makeQuery(id+"F8.imprint","IMPRINT",FACE,{"disambiguationData":[TD([[makeQuery(id+"F8.imprint","IMPRINT",EDGE,{"derivedFrom":sQuery(id+"F8.wireOp",EDGE,"E256")}),1.0]])]}),sQuery(id+"F11.wireOp",EDGE,"E332"),sQuery(id+"F12.wireOp",EDGE,"E396")])]});
            var Q1;
            Q1=makeQuery(id+"F17.opLoft","SWEPT_BODY",BODY,{"disambiguationData":[OSD([makeQuery(id+"F14.imprint","IMPRINT",FACE,{"disambiguationData":[TD([[makeQuery(id+"F14.imprint","IMPRINT",EDGE,{"derivedFrom":sQuery(id+"F14.wireOp",EDGE,"E448.bottom")}),1.0]])]}),makeQuery(id+"F16.imprint","IMPRINT",FACE,{"disambiguationData":[TD([[makeQuery(id+"F16.imprint","IMPRINT",EDGE,{"derivedFrom":sQuery(id+"F16.wireOp",EDGE,"E449.bottom")}),1.0]])]})])]});
            booleanBodies(context, id + "F18", {"operationType" : BooleanOperationType.SUBTRACTION, "tools" : qUnion([Q0]), "targets" : qUnion([Q1])});
        }
    });
